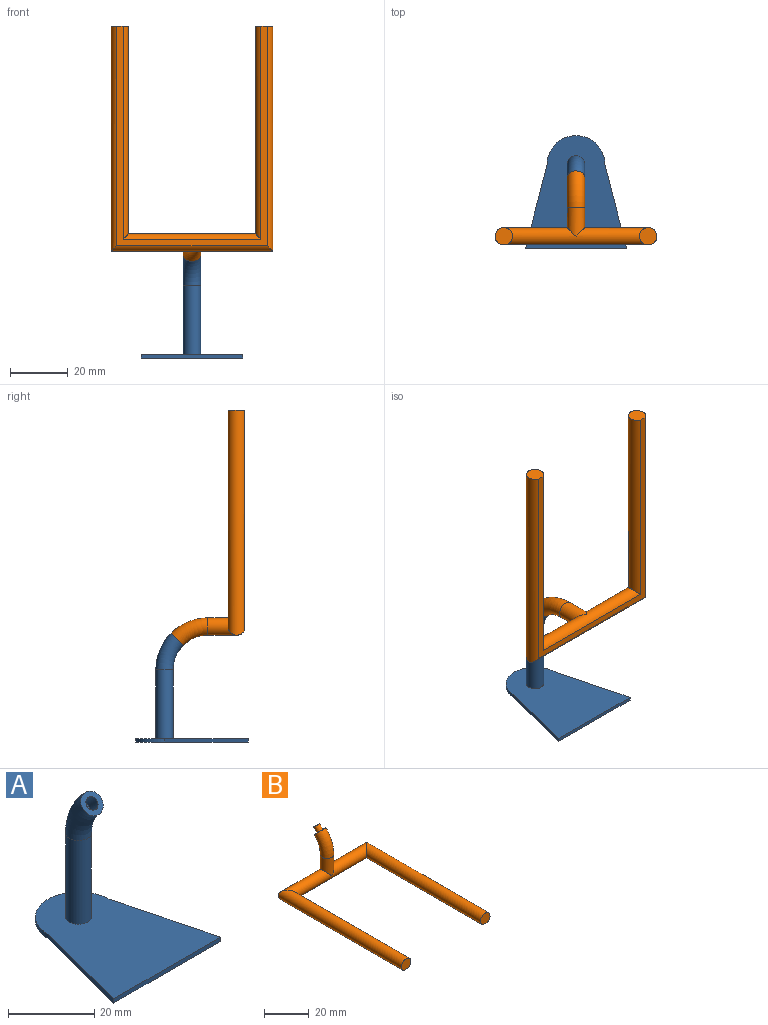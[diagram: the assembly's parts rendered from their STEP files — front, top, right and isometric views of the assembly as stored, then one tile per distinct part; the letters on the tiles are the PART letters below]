
ASSEMBLY  parts=2 mates=1
PART A: 15 faces, bbox 35x39x38.8 mm
  f0: cylinder r=3mm len=23.8mm, axis (0,0,1), area 448.6mm2, adj f2,f9
  f1: plane 6x4.24mm, normal (0,-0.71,0.71), area 20mm2, adj f2,f3
  f2: torus R=15mm, axis (1,0,0), area 222.1mm2, adj f0,f1
  f3: cylinder r=1.62mm len=5.13mm, axis (0,-0.71,0.71), area 40.8mm2, adj f1,f4
  f4: plane 3.25x2.3mm, normal (0,-0.71,0.71), area 8.3mm2, adj f3
  f5: plane 29.05x7.5mm, normal (-0.97,0.25,0), area 36mm2, adj f6,f8,f9,f10
  f6: cylinder r=10mm len=20mm, axis (0,0,-1), area 37.7mm2, adj f5,f7,f9,f10
  f7: plane 29.05x7.5mm, normal (0.97,0.25,0), area 36mm2, adj f6,f8,f9,f10
  f8: plane 35x1.2mm, normal (0,-1,0), area 42mm2, adj f5,f7,f9,f10
  f9: plane 39.05x35mm, normal (0,0,1), area 927.6mm2, adj f0,f5,f6,f7,f8
  f10: plane 39.05x35mm, normal (0,0,-1), area 945.7mm2, adj f5,f6,f7,f8,f11
  f11: cylinder r=1.8mm len=25mm, axis (0,0,1), area 282.7mm2, adj f10,f12
  f12: torus R=15mm, axis (1,0,0), area 73.2mm2, adj f11,f13,f14
  f13: cylinder r=2.82mm len=1.14mm, axis (0,-0.71,0.71), area 0.1mm2, adj f12,f14
  f14: plane 3.6x2.69mm, normal (0,0.71,-0.71), area 10.8mm2, adj f12,f13
PART B: 11 faces, bbox 56x82.6x26.6 mm
  f0: plane 6x5.77mm, normal (0,-1,0), area 27.9mm2, adj f2,f5
  f1: plane 6x5.77mm, normal (0,-1,0), area 27.9mm2, adj f4,f5
  f2: cylinder r=3mm len=78.02mm, axis (0,-1,0), area 1237mm2, adj f0,f3,f5
  f3: cylinder r=3mm len=56.05mm, axis (-1,0,0), area 788.7mm2, adj f2,f4,f5,f7
  f4: cylinder r=3mm len=78.02mm, axis (0,1,0), area 1237mm2, adj f1,f3,f5
  f5: plane 76.15x52.3mm, normal (0,0,-1), area 459.2mm2, adj f0,f1,f2,f3,f4
  f6: plane 6x4.24mm, normal (0,0.71,0.71), area 21.2mm2, adj f8,f9
  f7: cylinder r=3mm len=10mm, axis (0,0,1), area 152.5mm2, adj f3,f8
  f8: torus R=15mm, axis (-1,0,0), area 222.1mm2, adj f6,f7
  f9: cylinder r=1.5mm len=4.24mm, axis (0,-0.71,-0.71), area 28.3mm2, adj f6,f10
  f10: plane 3x2.12mm, normal (0,0.71,0.71), area 7.1mm2, adj f9
PLACE A at identity fixed
PLACE B rot(axis=(-1,0,0),90deg) t=(0,-25,40)mm
MATE fastened A.f3 <-> B.f9  axis (0,-0.71,0.71) through (0,-4.39,35.61)mm
